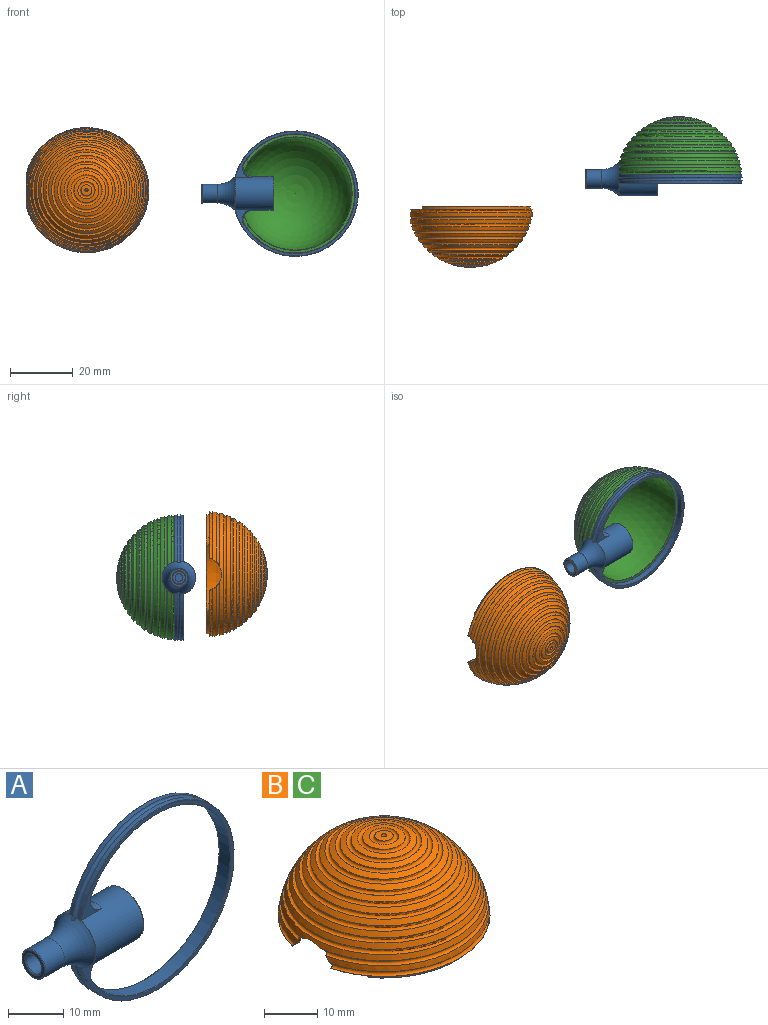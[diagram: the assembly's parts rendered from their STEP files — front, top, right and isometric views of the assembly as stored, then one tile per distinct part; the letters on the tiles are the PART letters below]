
ASSEMBLY  parts=3 mates=1
PART A: 34 faces, bbox 52.7x23.6x44.4 mm
  f0: plane 0.89x0.16mm, normal (0.26,0,-0.97), area 0mm2, adj f1,f4,f18,f30
  f1: sphere r=20mm, area 104.5mm2, adj f0,f2,f18,f28,f30
  f2: plane 0.89x0.16mm, normal (0.26,0,0.97), area 0mm2, adj f1,f4,f18,f30
  f3: plane 0.89x0.16mm, normal (0.26,0,-0.97), area 0mm2, adj f4,f16,f18,f29
  f4: torus R=10.9mm, axis (1,0,0), area 146.5mm2, adj f0,f2,f3,f13,f17,f18,f29,f30
  f5: plane 39.7x39.03mm, normal (0,-1,0), area 94.4mm2, adj f12,f24,f25,f26,f27
  f6: plane 39.7x39.03mm, normal (0,1,0), area 94.4mm2, adj f12,f21,f22,f23,f28
  f7: cylinder r=2mm len=10.8mm, axis (1,0,0), area 134.1mm2, adj f8,f18,f33
  f8: plane 4x4mm, normal (-1,0,0), area 7.7mm2, adj f7,f9
  f9: cylinder r=1.25mm len=10mm, axis (1,0,0), area 78.5mm2, adj f8,f10
  f10: plane 2.5x2.5mm, normal (-1,0,0), area 4.9mm2, adj f9
  f11: plane 10.3x10.3mm, normal (1,0,0), area 83.3mm2, adj f31
  f12: cylinder r=5.35mm len=12.14mm, axis (1,0,0), area 374.5mm2, adj f5,f6,f19,f20,f21,f23,f24,f26
  f13: cylinder r=3mm len=6mm, axis (1,0,0), area 90.5mm2, adj f4,f32
  f14: plane 5.6x5.6mm, normal (-1,0,0), area 9.4mm2, adj f32,f33
  f15: cylinder r=19mm len=38mm, axis (0,1,0), area 276.2mm2, adj f19,f20,f22,f25
  f16: sphere r=20mm, area 104.5mm2, adj f3,f17,f18,f27,f29
  f17: plane 0.89x0.16mm, normal (0.26,0,0.97), area 0mm2, adj f4,f16,f18,f29
  f18: torus R=20mm, axis (0,1,0), area 196.1mm2, adj f0,f1,f2,f3,f4,f7,f16,f17
  f19: bspline ~6.46x5.36mm, area 16mm2, adj f12,f15,f21,f24
  f20: bspline ~6.46x5.36mm, area 16mm2, adj f12,f15,f23,f26
  f21: bspline ~5.12x3.51mm, area 0.8mm2, adj f6,f12,f19,f22
  f22: torus R=19.1mm, axis (0,-1,0), area 15.6mm2, adj f6,f15,f21,f23
  f23: bspline ~5.12x3.51mm, area 0.8mm2, adj f6,f12,f20,f22
  f24: bspline ~5.12x3.51mm, area 0.8mm2, adj f5,f12,f19,f25
  f25: torus R=19.1mm, axis (0,-1,0), area 15.6mm2, adj f5,f15,f24,f26
  f26: bspline ~5.12x3.51mm, area 0.8mm2, adj f5,f12,f20,f25
  f27: torus R=19.85mm, axis (0,-1,0), area 17.2mm2, adj f5,f12,f16,f29
  f28: torus R=19.85mm, axis (0,-1,0), area 17.2mm2, adj f1,f6,f12,f30
  f29: torus R=5.25mm, axis (-1,0,0), area 1.1mm2, adj f3,f4,f12,f16,f17,f27
  f30: torus R=5.25mm, axis (-1,0,0), area 1.1mm2, adj f0,f1,f2,f4,f12,f28
  f31: torus R=5.15mm, axis (-1,0,0), area 10.4mm2, adj f11,f12
  f32: torus R=2.8mm, axis (-1,0,0), area 5.8mm2, adj f13,f14
  f33: torus R=2.2mm, axis (-1,0,0), area 4.1mm2, adj f7,f14
PART B: 38 faces, bbox 43.3x43.8x19.7 mm
  f0: plane 37.8x34.22mm, normal (0,0,-1), area 76.1mm2, adj f32,f34,f36,f37
  f1: sphere r=18mm, area 1919.4mm2, adj f2,f32,f33,f36,f37
  f2: plane 39.68x39.01mm, normal (0,0,-1), area 105.8mm2, adj f1,f3,f31,f33,f35,f36,f37
  f3: cylinder r=19mm len=38mm, axis (0,0,-1), area 84.9mm2, adj f2,f34,f36,f37
  f4: torus R=19.89mm, axis (0,0,-1), area 176.1mm2, adj f6,f31,f35
  f5: torus R=19.53mm, axis (0,0,-1), area 178.1mm2, adj f6,f7,f31
  f6: sphere r=20mm, area 145mm2, adj f4,f5,f31
  f7: sphere r=20mm, area 150.1mm2, adj f5,f8,f31
  f8: torus R=18.92mm, axis (0,0,-1), area 182.3mm2, adj f7,f9
  f9: sphere r=20mm, area 146.1mm2, adj f8,f10
  f10: torus R=18.07mm, axis (0,0,-1), area 174.1mm2, adj f9,f11
  f11: sphere r=20mm, area 138.5mm2, adj f10,f12
  f12: torus R=16.99mm, axis (0,0,-1), area 163.7mm2, adj f11,f13
  f13: sphere r=20mm, area 129.1mm2, adj f12,f14
  f14: torus R=15.69mm, axis (0,0,-1), area 151.2mm2, adj f13,f15
  f15: sphere r=20mm, area 118.1mm2, adj f14,f16
  f16: torus R=14.2mm, axis (0,0,-1), area 136.8mm2, adj f15,f17
  f17: sphere r=20mm, area 105.5mm2, adj f16,f18
  f18: torus R=12.52mm, axis (0,0,-1), area 120.7mm2, adj f17,f19
  f19: sphere r=20mm, area 91.7mm2, adj f18,f20
  f20: torus R=10.69mm, axis (0,0,-1), area 103mm2, adj f19,f21
  f21: sphere r=20mm, area 76.7mm2, adj f20,f22
  f22: torus R=8.72mm, axis (0,0,-1), area 84mm2, adj f21,f23
  f23: sphere r=20mm, area 60.7mm2, adj f22,f24
  f24: torus R=6.64mm, axis (0,0,-1), area 64mm2, adj f23,f25
  f25: sphere r=20mm, area 43.9mm2, adj f24,f26
  f26: torus R=4.47mm, axis (0,0,-1), area 43.1mm2, adj f25,f27
  f27: sphere r=20mm, area 26.6mm2, adj f26,f28
  f28: torus R=2.25mm, axis (0,0,-1), area 21.7mm2, adj f27,f29
  f29: sphere r=20mm, area 8.9mm2, adj f28,f30
  f30: sphere r=0.5mm, area 1.6mm2, adj f29
  f31: cylinder r=5.35mm len=10.27mm, axis (1,0,0), area 25.5mm2, adj f2,f4,f5,f6,f7,f33,f35
  f32: torus R=18.09mm, axis (0,0,1), area 14.3mm2, adj f0,f1,f36,f37
  f33: torus R=5.45mm, axis (1,0,0), area 1.8mm2, adj f1,f2,f31
  f34: torus R=18.9mm, axis (0,0,1), area 14.8mm2, adj f0,f3,f36,f37
  f35: torus R=19.84mm, axis (0,0,-1), area 17.2mm2, adj f2,f4,f31
  f36: cylinder r=6mm len=2.28mm, axis (0,0,-1), area 2.2mm2, adj f0,f1,f2,f3,f32,f34
  f37: cylinder r=6mm len=2.28mm, axis (0,0,-1), area 2.2mm2, adj f0,f1,f2,f3,f32,f34
PART C: same geometry as B
PLACE A rot(axis=(1,0,0),180deg) t=(-15.91,-144.43,80.29)mm
PLACE B rot(axis=(1,0,0),90deg) t=(-82.47,-152.67,81.4)mm
PLACE C rot(axis=(-1,0,0),90deg) t=(-15.91,-144.53,80.29)mm
MATE fastened C.f3 <-> A.f27  axis (0,-1,0) through (-15.91,-143.03,80.29)mm
